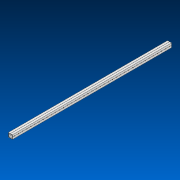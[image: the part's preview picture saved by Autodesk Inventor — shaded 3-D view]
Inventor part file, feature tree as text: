
AUTODESK INVENTOR PART (.ipt)
format: ipt  version: 2022.2 (Build 262287000, 287)  size: 826,368 bytes
history: native  units: in
note: dims shown in document units (in); Inventor stores cm internally (conversion verified against a paired STEP export)
features: other x39, extrude x1, pattern_linear x1, sketch x1, pattern_circular x1
ambient origin geometry x8: Origin, YZ Plane, XZ Plane, XY Plane, X Axis, Y Axis, Z Axis, Center Point
bodies: Solid1 (feature_tree)
feature tree (43):
  extrude  "Extrusion1"  Depth=1.0in
  other  "Work Axis1"
  pattern_linear  "Rectangular Pattern1"  Spacing1=0.0in  [1 undecoded]
  sketch  "Sketch1"  dims[d0=1.0in d1=20.0in d2=0.0in d3=15.3543in d5=1.0in]
  other  "Work Axis2"
  other  "Work Axis3"
  other  "Work Axis4"
  other  "Work Axis5"
  other  "Work Axis6"
  other  "Work Axis7"
  other  "Work Axis8"
  other  "Work Axis9"
  other  "Work Axis10"
  other  "Work Axis11"
  other  "Work Axis12"
  other  "Work Axis13"
  other  "Work Axis14"
  other  "Work Axis15"
  other  "Work Axis16"
  other  "Work Axis17"
  other  "Work Axis18"
  other  "Work Axis19"
  other  "Work Axis20"
  other  "Work Axis21"
  other  "Work Axis22"
  other  "Work Axis23"
  other  "Work Axis24"
  other  "Work Axis25"
  other  "Work Axis26"
  other  "Work Axis27"
  other  "Work Axis28"
  other  "Work Axis29"
  other  "Work Axis30"
  other  "Work Axis31"
  other  "Work Axis32"
  other  "Work Axis33"
  other  "Work Axis34"
  other  "Work Axis35"
  other  "Work Axis36"
  other  "Work Axis37"
  other  "Work Axis38"
  other  "Work Axis39"
  pattern_circular  "CirPattern2"
note: 1 required parameter value undecoded (feature->parameter linkage not recoverable at this tier; creation-order binding heuristic only, values carry confidence <= 0.55)
